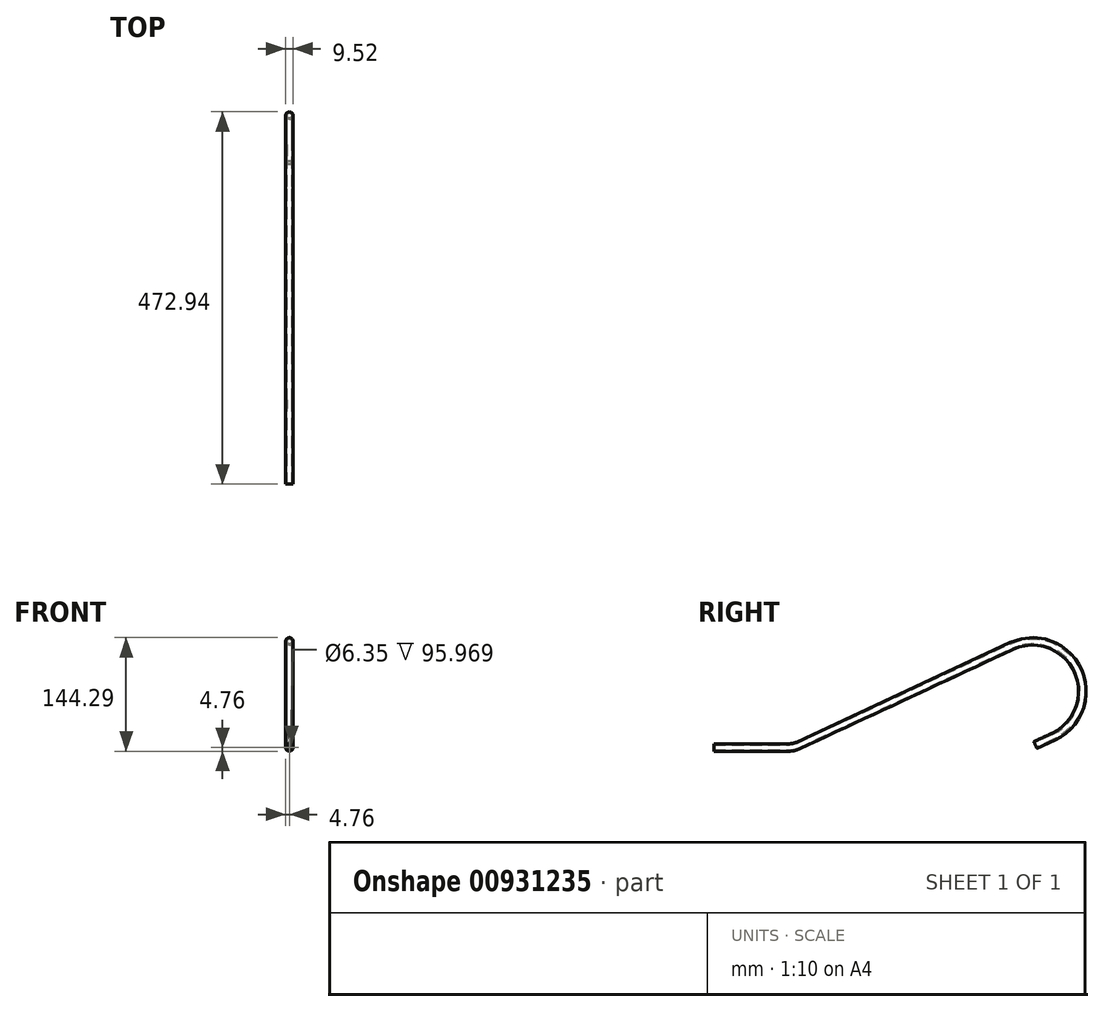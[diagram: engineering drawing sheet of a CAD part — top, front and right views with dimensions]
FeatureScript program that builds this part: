
annotation { "Feature Type Name" : "Feature", "Feature Type Description" : "" }
export const myFeature = defineFeature(function(context is Context, id is Id, definition is map)
    precondition{}
    {
        {
            var Q0;
            Q0=qCreatedBy(makeId("Right.planeOp"),FACE);
            var sketch = newSketch(context, id + "F0", { "sketchPlane" : qUnion([Q0])});
            skLineSegment(sketch, "E0", {"start": v(0, 0) * mm, "end": v(95.97, 0) * mm});
            skLineSegment(sketch, "E1", {"start": v(106.7, 2.38) * mm, "end": v(377.84, 128.81) * mm});
            skLineSegment(sketch, "E2.0", {"start": v(408.5, 2.98) * mm, "end": v(431.52, 13.71) * mm});
            skArc(sketch, "E3", {"start": v(431.52, 13.71) * mm, "mid": v(462.23, 98.1) * mm, "end": v(377.84, 128.81) * mm});
            skPoint(sketch, "E4.visualSharp", {"position": v(101.6, 0) * mm});
            skArc(sketch, "E4.filletArc", {"start": v(95.97, 0) * mm, "mid": v(101.47, 0.6) * mm, "end": v(106.7, 2.38) * mm});
            skSolve(sketch);
        }
        {
            var Q0;
            Q0=qCreatedBy(makeId("Front.planeOp"),FACE);
            var sketch = newSketch(context, id + "F1", { "sketchPlane" : qUnion([Q0])});
            skCircle(sketch, "E5", {"center": v(0, 0) * mm, "radius": 4.76 * mm});
            skSolve(sketch);
        }
        {
            var Q0;
            Q0=makeQuery(id+"F1.imprint","IMPRINT",FACE,{"disambiguationData":[TD([[makeQuery(id+"F1.imprint","IMPRINT",EDGE,{"derivedFrom":sQuery(id+"F1.wireOp",EDGE,"E5")}),1.0]])]});
            var Q1;
            Q1=sQuery(id+"F0.wireOp",EDGE,"E0");
            var Q2;
            Q2=sQuery(id+"F0.wireOp",EDGE,"E1");
            var Q3;
            Q3=sQuery(id+"F0.wireOp",EDGE,"E3");
            var Q4;
            Q4=sQuery(id+"F0.wireOp",EDGE,"E2.0");
            var Q5;
            Q5=sQuery(id+"F0.wireOp",EDGE,"E4.filletArc");
            sweep(context, id + "F2", {"profiles" : qUnion([Q0]), "path" : qUnion([Q1, Q2, Q3, Q4, Q5])});
        }
        {
            var Q0;
            Q0=makeQuery(id+"F2.opSweep","CAP_FACE",FACE,{"disambiguationData":[OSD([sQuery(id+"F0.wireOp",VERTEX,"E0.start"),sQuery(id+"F1.wireOp",EDGE,"E5")])],"isStart":true});
            var Q1;
            Q1=makeQuery(id+"F2.opSweep","CAP_FACE",FACE,{"disambiguationData":[OSD([sQuery(id+"F0.wireOp",VERTEX,"E2.0.start"),sQuery(id+"F1.wireOp",EDGE,"E5")])],"isStart":false});
            shell(context, id + "F3", {"entities" : qUnion([Q0, Q1]), "thickness" : 1.59 * mm});
        }
    });
